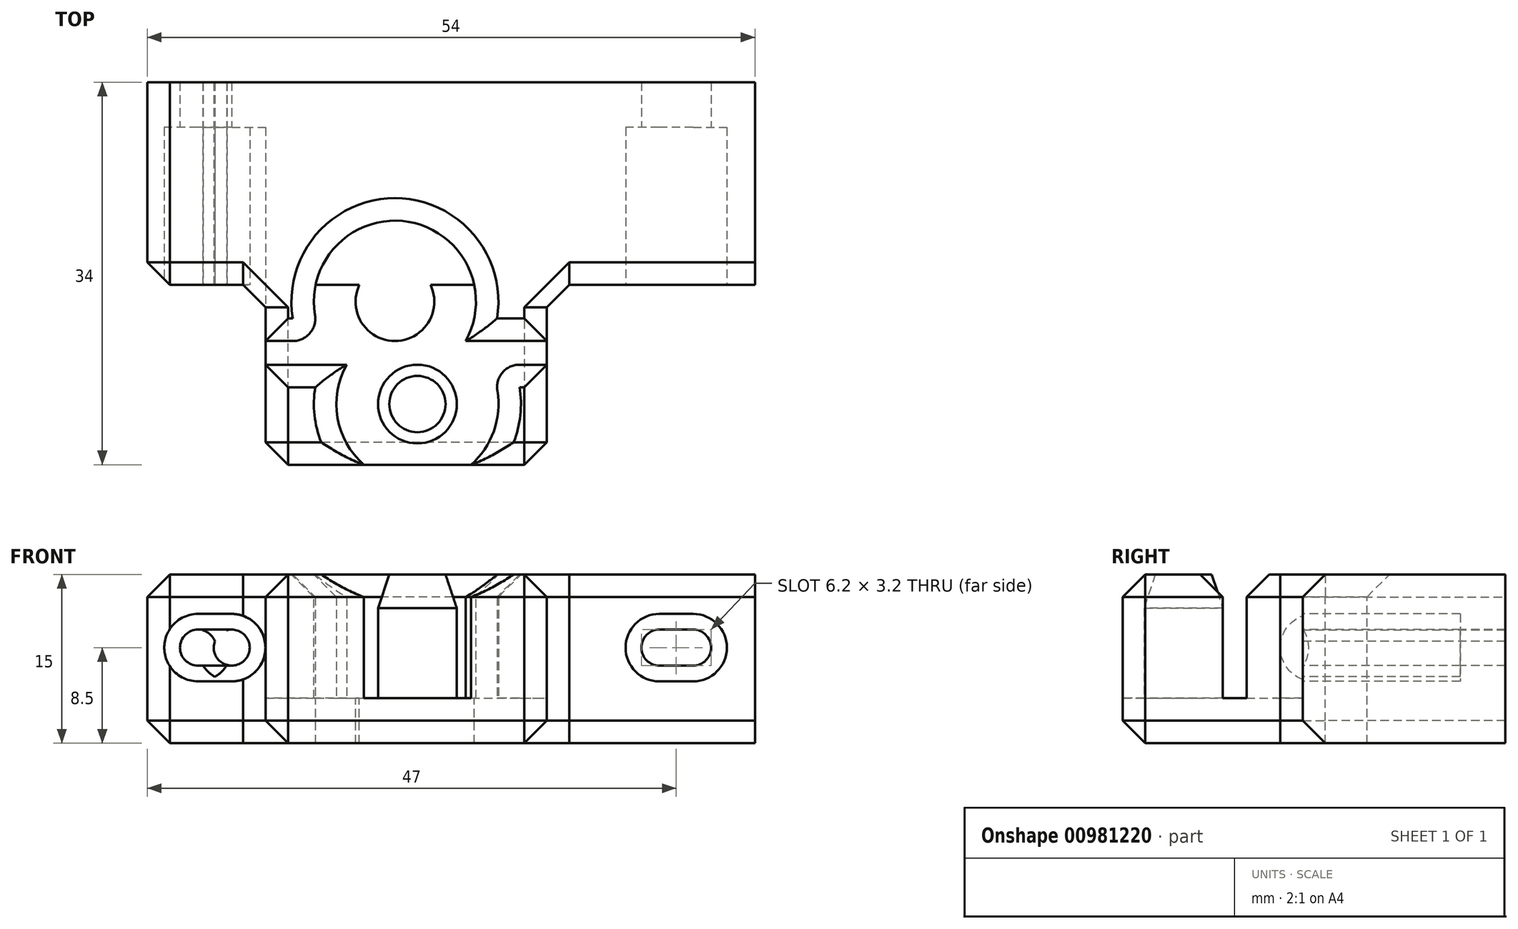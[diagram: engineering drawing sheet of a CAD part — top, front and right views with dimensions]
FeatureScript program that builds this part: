
annotation { "Feature Type Name" : "Feature", "Feature Type Description" : "" }
export const myFeature = defineFeature(function(context is Context, id is Id, definition is map)
    precondition{}
    {
        {
            var Q0;
            Q0=qCreatedBy(makeId("Top.planeOp"),FACE);
            var sketch = newSketch(context, id + "F0", { "sketchPlane" : qUnion([Q0])});
            skLineSegment(sketch, "E0.bottom", {"start": v(0, 0) * mm, "end": v(54, 0) * mm});
            skLineSegment(sketch, "E0.top", {"start": v(0, 10) * mm, "end": v(54, 10) * mm});
            skLineSegment(sketch, "E0.left", {"start": v(0, 0) * mm, "end": v(0, 10) * mm});
            skLineSegment(sketch, "E0.right", {"start": v(54, 0) * mm, "end": v(54, 10) * mm});
            skLineSegment(sketch, "E1.bottom", {"start": v(10.5, 0) * mm, "end": v(35.5, 0) * mm});
            skLineSegment(sketch, "E1.top", {"start": v(10.5, -16) * mm, "end": v(35.5, -16) * mm});
            skLineSegment(sketch, "E1.left", {"start": v(10.5, 0) * mm, "end": v(10.5, -16) * mm});
            skLineSegment(sketch, "E1.right", {"start": v(35.5, 0) * mm, "end": v(35.5, -16) * mm});
            skLineSegment(sketch, "E2", {"start": v(10.5, -5) * mm, "end": v(12.92, -5) * mm});
            skLineSegment(sketch, "E3", {"start": v(33.08, -7.1) * mm, "end": v(35.5, -7.1) * mm});
            skCircle(sketch, "E4", {"center": v(22, -1.5) * mm, "radius": 3.5 * mm});
            skCircle(sketch, "E5", {"center": v(24, -10.6) * mm, "radius": 3.5 * mm});
            skArc(sketch, "E6", {"start": v(28.76, -16) * mm, "mid": v(30.78, -13.02) * mm, "end": v(31.1, -9.43) * mm});
            skArc(sketch, "E7", {"start": v(28.3, -5) * mm, "mid": v(23.23, 5.6) * mm, "end": v(14.9, -2.67) * mm});
            skLineSegment(sketch, "E8", {"start": v(22, -1.5) * mm, "end": v(22, -19) * mm, "construction": true});
            skLineSegment(sketch, "E9", {"start": v(22, -19) * mm, "end": v(24, -19) * mm, "construction": true});
            skLineSegment(sketch, "E10", {"start": v(24, -19) * mm, "end": v(24, -10.6) * mm, "construction": true});
            skPoint(sketch, "E11", {"position": v(23, -16) * mm});
            skPoint(sketch, "E12", {"position": v(23, -19) * mm});
            skArc(sketch, "E13.trimOffspring", {"start": v(17.7, -7.1) * mm, "mid": v(16.9, -11.82) * mm, "end": v(19.24, -16) * mm});
            skPoint(sketch, "E14.newPointA", {"position": v(35.5, -5) * mm});
            skArc(sketch, "E14.filletArc", {"start": v(12.92, -5) * mm, "mid": v(14.45, -4.3) * mm, "end": v(14.9, -2.67) * mm});
            skArc(sketch, "E15.filletArc", {"start": v(33.08, -7.1) * mm, "mid": v(31.55, -7.8) * mm, "end": v(31.1, -9.43) * mm});
            skLineSegment(sketch, "E16", {"start": v(17.7, -7.1) * mm, "end": v(10.5, -7.1) * mm});
            skLineSegment(sketch, "E17", {"start": v(28.3, -5) * mm, "end": v(35.5, -5) * mm});
            skLineSegment(sketch, "E18", {"start": v(0, 10) * mm, "end": v(0, 18) * mm});
            skLineSegment(sketch, "E19", {"start": v(0, 18) * mm, "end": v(54, 18) * mm});
            skLineSegment(sketch, "E20", {"start": v(54, 18) * mm, "end": v(54, 10) * mm});
            skSolve(sketch);
        }
        {
            var Q0;
            Q0=makeQuery(id+"F0.imprint","IMPRINT",FACE,{"disambiguationData":[TD([[makeQuery(id+"F0.imprint","IMPRINT",EDGE,{"derivedFrom":sQuery(id+"F0.wireOp",EDGE,"E0.top")}),-1.0]])]});
            var Q1;
            {var subQ6=sQuery(id+"F0.wireOp",EDGE,"E2");Q1=makeQuery(id+"F0.imprint","IMPRINT",FACE,{"disambiguationData":[TD([[makeQuery(id+"F0.imprint","IMPRINT",EDGE,{"derivedFrom":subQ6}),1.0]])]});}
            var Q2;
            {var subQ3=sQuery(id+"F0.wireOp",EDGE,"E13.trimOffspring");Q2=makeQuery(id+"F0.imprint","IMPRINT",FACE,{"disambiguationData":[TD([[makeQuery(id+"F0.imprint","IMPRINT",EDGE,{"derivedFrom":subQ3}),-1.0]])]});}
            var Q3;
            {var subQ1=sQuery(id+"F0.wireOp",EDGE,"E3");Q3=makeQuery(id+"F0.imprint","IMPRINT",FACE,{"disambiguationData":[TD([[makeQuery(id+"F0.imprint","IMPRINT",EDGE,{"derivedFrom":subQ1}),-1.0]])]});}
            var Q4;
            {var subQ5=sQuery(id+"F0.wireOp",EDGE,"E17");Q4=makeQuery(id+"F0.imprint","IMPRINT",FACE,{"disambiguationData":[TD([[makeQuery(id+"F0.imprint","IMPRINT",EDGE,{"derivedFrom":subQ5}),1.0]])]});}
            var Q5;
            {var subQ13=sQuery(id+"F0.wireOp",EDGE,"E2");Q5=makeQuery(id+"F0.imprint","IMPRINT",FACE,{"disambiguationData":[TD([[makeQuery(id+"F0.imprint","IMPRINT",EDGE,{"derivedFrom":subQ13}),-1.0]])]});}
            var Q6;
            {var subQ0=sQuery(id+"F0.wireOp",EDGE,"E4");var subQ1=sQuery(id+"F0.wireOp",EDGE,"E1.bottom");var subQ2=makeQuery(id+"F0.imprint","INTERSECT",VERTEX,{"disambiguationData":[OD(0.0)],"derivedFrom":[subQ1,subQ0]});Q6=makeQuery(id+"F0.imprint","IMPRINT",FACE,{"disambiguationData":[TD([[makeQuery(id+"F0.imprint","IMPRINT",EDGE,{"disambiguationData":[TD([[subQ2,-1.0]])],"derivedFrom":subQ1}),-1.0]])]});}
            var Q7;
            Q7=makeQuery(id+"F0.imprint","IMPRINT",FACE,{"disambiguationData":[TD([[makeQuery(id+"F0.imprint","IMPRINT",EDGE,{"derivedFrom":sQuery(id+"F0.wireOp",EDGE,"E5")}),1.0]])]});
            var Q8;
            {var subQ0=sQuery(id+"F0.wireOp",EDGE,"E4");var subQ1=sQuery(id+"F0.wireOp",EDGE,"E1.bottom");var subQ2=makeQuery(id+"F0.imprint","INTERSECT",VERTEX,{"disambiguationData":[OD(0.0)],"derivedFrom":[subQ1,subQ0]});Q8=makeQuery(id+"F0.imprint","IMPRINT",FACE,{"disambiguationData":[TD([[makeQuery(id+"F0.imprint","IMPRINT",EDGE,{"disambiguationData":[TD([[subQ2,-1.0]])],"derivedFrom":subQ1}),1.0]])]});}
            var Q9;
            {var subQ0=sQuery(id+"F0.wireOp",EDGE,"E7");var subQ1=sQuery(id+"F0.wireOp",EDGE,"E1.bottom");var subQ2=makeQuery(id+"F0.imprint","INTERSECT",VERTEX,{"disambiguationData":[OD(0.0)],"derivedFrom":[subQ1,subQ0]});Q9=makeQuery(id+"F0.imprint","IMPRINT",FACE,{"disambiguationData":[TD([[makeQuery(id+"F0.imprint","IMPRINT",EDGE,{"disambiguationData":[TD([[subQ2,-1.0]])],"derivedFrom":subQ1}),1.0]])]});}
            var Q10;
            Q10=makeQuery(id+"F0.imprint","IMPRINT",FACE,{"disambiguationData":[TD([[makeQuery(id+"F0.imprint","IMPRINT",EDGE,{"derivedFrom":sQuery(id+"F0.wireOp",EDGE,"E0.top")}),1.0]])]});
            extrude(context, id + "F1", {"entities" : qUnion([Q0, Q1, Q2, Q3, Q4, Q5, Q6, Q7, Q8, Q9, Q10]), "oppositeDirection" : true, "depth" : 4 * mm, "offsetDistance" : 25 * mm});
        }
        {
            var Q0;
            Q0=makeQuery(id+"F0.imprint","IMPRINT",FACE,{"disambiguationData":[TD([[makeQuery(id+"F0.imprint","IMPRINT",EDGE,{"derivedFrom":sQuery(id+"F0.wireOp",EDGE,"E0.top")}),-1.0]])]});
            var Q1;
            {var subQ5=sQuery(id+"F0.wireOp",EDGE,"E17");Q1=makeQuery(id+"F0.imprint","IMPRINT",FACE,{"disambiguationData":[TD([[makeQuery(id+"F0.imprint","IMPRINT",EDGE,{"derivedFrom":subQ5}),1.0]])]});}
            var Q2;
            {var subQ6=sQuery(id+"F0.wireOp",EDGE,"E2");Q2=makeQuery(id+"F0.imprint","IMPRINT",FACE,{"disambiguationData":[TD([[makeQuery(id+"F0.imprint","IMPRINT",EDGE,{"derivedFrom":subQ6}),1.0]])]});}
            var Q3;
            {var subQ3=sQuery(id+"F0.wireOp",EDGE,"E13.trimOffspring");Q3=makeQuery(id+"F0.imprint","IMPRINT",FACE,{"disambiguationData":[TD([[makeQuery(id+"F0.imprint","IMPRINT",EDGE,{"derivedFrom":subQ3}),-1.0]])]});}
            var Q4;
            {var subQ1=sQuery(id+"F0.wireOp",EDGE,"E3");Q4=makeQuery(id+"F0.imprint","IMPRINT",FACE,{"disambiguationData":[TD([[makeQuery(id+"F0.imprint","IMPRINT",EDGE,{"derivedFrom":subQ1}),-1.0]])]});}
            var Q5;
            Q5=makeQuery(id+"F0.imprint","IMPRINT",FACE,{"disambiguationData":[TD([[makeQuery(id+"F0.imprint","IMPRINT",EDGE,{"derivedFrom":sQuery(id+"F0.wireOp",EDGE,"E5")}),1.0]])]});
            var Q6;
            {var subQ0=sQuery(id+"F0.wireOp",EDGE,"E4");var subQ1=sQuery(id+"F0.wireOp",EDGE,"E1.bottom");var subQ2=makeQuery(id+"F0.imprint","INTERSECT",VERTEX,{"disambiguationData":[OD(0.0)],"derivedFrom":[subQ1,subQ0]});Q6=makeQuery(id+"F0.imprint","IMPRINT",FACE,{"disambiguationData":[TD([[makeQuery(id+"F0.imprint","IMPRINT",EDGE,{"disambiguationData":[TD([[subQ2,-1.0]])],"derivedFrom":subQ1}),-1.0]])]});}
            var Q7;
            {var subQ0=sQuery(id+"F0.wireOp",EDGE,"E4");var subQ1=sQuery(id+"F0.wireOp",EDGE,"E1.bottom");var subQ2=makeQuery(id+"F0.imprint","INTERSECT",VERTEX,{"disambiguationData":[OD(0.0)],"derivedFrom":[subQ1,subQ0]});Q7=makeQuery(id+"F0.imprint","IMPRINT",FACE,{"disambiguationData":[TD([[makeQuery(id+"F0.imprint","IMPRINT",EDGE,{"disambiguationData":[TD([[subQ2,-1.0]])],"derivedFrom":subQ1}),1.0]])]});}
            var Q8;
            Q8=makeQuery(id+"F0.imprint","IMPRINT",FACE,{"disambiguationData":[TD([[makeQuery(id+"F0.imprint","IMPRINT",EDGE,{"derivedFrom":sQuery(id+"F0.wireOp",EDGE,"E0.top")}),1.0]])]});
            extrude(context, id + "F2", {"entities" : qUnion([Q0, Q1, Q2, Q3, Q4, Q5, Q6, Q7, Q8]), "operationType" : NewBodyOperationType.ADD, "depth" : 11 * mm, "offsetDistance" : 25 * mm});
        }
        {
            var Q0;
            Q0=makeQuery(id+"F2.opExtrude","CAP_EDGE",EDGE,{"disambiguationData":[OSD([sQuery(id+"F0.wireOp",EDGE,"E2")])],"isStart":false});
            var Q1;
            Q1=makeQuery(id+"F2.opExtrude","CAP_EDGE",EDGE,{"disambiguationData":[OSD([sQuery(id+"F0.wireOp",EDGE,"E17")])],"isStart":false});
            var Q2;
            Q2=makeQuery(id+"F2.opExtrude","CAP_EDGE",EDGE,{"disambiguationData":[OSD([sQuery(id+"F0.wireOp",EDGE,"E3")])],"isStart":false});
            var Q3;
            Q3=makeQuery(id+"F2.opExtrude","CAP_EDGE",EDGE,{"disambiguationData":[OSD([sQuery(id+"F0.wireOp",EDGE,"E13.trimOffspring")])],"isStart":false});
            var Q4;
            Q4=makeQuery(id+"F2.opExtrude","CAP_EDGE",EDGE,{"disambiguationData":[OSD([sQuery(id+"F0.wireOp",EDGE,"E16")])],"isStart":false});
            chamfer(context, id + "F3", {"entities" : qUnion([Q0, Q1, Q2, Q3, Q4]), "width" : 2 * mm, "tangentPropagation" : true});
        }
        {
            var Q0;
            Q0=makeQuery(id+"F2.opExtrude","CAP_FACE",FACE,{"disambiguationData":[OSD([sQuery(id+"F0.wireOp",EDGE,"E4")])],"isStart":false});
            var Q1;
            Q1=makeQuery(id+"F2.opExtrude","CAP_EDGE",EDGE,{"disambiguationData":[OSD([sQuery(id+"F0.wireOp",EDGE,"E5")])],"isStart":false});
            chamfer(context, id + "F4", {"entities" : qUnion([Q0, Q1]), "chamferType" : ChamferType.TWO_OFFSETS, "width1" : 1 * mm, "oppositeDirection" : false, "width2" : 3 * mm, "tangentPropagation" : true});
        }
        {
            var Q0;
            {var subQ0=sQuery(id+"F0.wireOp",EDGE,"E0.bottom");var subQ1=makeQuery(id+"F0.imprint","IMPRINT",EDGE,{"disambiguationData":[TD([[makeQuery(id+"F0.imprint","INTERSECT",VERTEX,{"derivedFrom":[subQ0,sQuery(id+"F0.wireOp",EDGE,"E0.right")]}),1.0]])],"derivedFrom":subQ0});Q0=makeQuery(id+"F2.boolean.opBoolean","MERGE",FACE,{"derivedFrom":[makeQuery(id+"F1.opExtrude","SWEPT_FACE",FACE,{"disambiguationData":[OSD([subQ0]),TDD([subQ1])]}),makeQuery(id+"F2.opExtrude","SWEPT_FACE",FACE,{"disambiguationData":[OSD([subQ0]),TDD([subQ1])]})]});}
            var sketch = newSketch(context, id + "F5", { "sketchPlane" : qUnion([Q0])});
            skCircle(sketch, "E21", {"center": v(4.5, 4.5) * mm, "radius": 1.6 * mm});
            skCircle(sketch, "E22", {"center": v(4.5, 4.5) * mm, "radius": 3 * mm});
            skCircle(sketch, "E23", {"center": v(48.5, 4.5) * mm, "radius": 1.6 * mm});
            skCircle(sketch, "E24", {"center": v(48.5, 4.5) * mm, "radius": 3 * mm});
            skCircle(sketch, "E25", {"center": v(7.5, 4.5) * mm, "radius": 1.6 * mm});
            skCircle(sketch, "E26", {"center": v(7.5, 4.5) * mm, "radius": 3 * mm});
            skCircle(sketch, "E27", {"center": v(45.5, 4.5) * mm, "radius": 1.6 * mm});
            skCircle(sketch, "E28", {"center": v(45.5, 4.5) * mm, "radius": 3 * mm});
            skLineSegment(sketch, "E29", {"start": v(4.5, 6.1) * mm, "end": v(7.5, 6.1) * mm});
            skLineSegment(sketch, "E30", {"start": v(7.5, 2.9) * mm, "end": v(4.5, 2.9) * mm});
            skLineSegment(sketch, "E31", {"start": v(45.5, 2.9) * mm, "end": v(48.5, 2.9) * mm});
            skLineSegment(sketch, "E32", {"start": v(48.5, 6.1) * mm, "end": v(45.5, 6.1) * mm});
            skLineSegment(sketch, "E33", {"start": v(45.5, 7.5) * mm, "end": v(48.5, 7.5) * mm});
            skLineSegment(sketch, "E34", {"start": v(48.5, 1.5) * mm, "end": v(45.5, 1.5) * mm});
            skLineSegment(sketch, "E35", {"start": v(7.5, 7.5) * mm, "end": v(4.5, 7.5) * mm});
            skLineSegment(sketch, "E36", {"start": v(4.5, 1.5) * mm, "end": v(7.5, 1.5) * mm});
            skSolve(sketch);
        }
        {
            var Q0;
            {var subQ0=sQuery(id+"F5.wireOp",EDGE,"E21");var subQ1=makeQuery(id+"F5.imprint","INTERSECT",VERTEX,{"derivedFrom":[subQ0,sQuery(id+"F5.wireOp",EDGE,"E29")]});Q0=makeQuery(id+"F5.imprint","IMPRINT",FACE,{"disambiguationData":[TD([[makeQuery(id+"F5.imprint","IMPRINT",EDGE,{"disambiguationData":[TD([[subQ1,1.0]])],"derivedFrom":subQ0}),1.0]])]});}
            var Q1;
            {var subQ0=sQuery(id+"F5.wireOp",EDGE,"E26");var subQ1=sQuery(id+"F5.wireOp",EDGE,"E21");var subQ2=makeQuery(id+"F5.imprint","INTERSECT",VERTEX,{"disambiguationData":[OD(0.0)],"derivedFrom":[subQ1,subQ0]});Q1=makeQuery(id+"F5.imprint","IMPRINT",FACE,{"disambiguationData":[TD([[makeQuery(id+"F5.imprint","IMPRINT",EDGE,{"disambiguationData":[TD([[subQ2,1.0]])],"derivedFrom":subQ1}),1.0]])]});}
            var Q2;
            {var subQ0=sQuery(id+"F5.wireOp",EDGE,"E25");var subQ1=sQuery(id+"F5.wireOp",EDGE,"E21");var subQ2=makeQuery(id+"F5.imprint","INTERSECT",VERTEX,{"disambiguationData":[OD(0.0)],"derivedFrom":[subQ1,subQ0]});Q2=makeQuery(id+"F5.imprint","IMPRINT",FACE,{"disambiguationData":[TD([[makeQuery(id+"F5.imprint","IMPRINT",EDGE,{"disambiguationData":[TD([[subQ2,1.0]])],"derivedFrom":subQ1}),-1.0]])]});}
            var Q3;
            {var subQ1=sQuery(id+"F5.wireOp",EDGE,"E21");var subQ5=sQuery(id+"F5.wireOp",EDGE,"E26");var subQ6=makeQuery(id+"F5.imprint","INTERSECT",VERTEX,{"disambiguationData":[OD(0.0)],"derivedFrom":[subQ1,subQ5]});Q3=makeQuery(id+"F5.imprint","IMPRINT",FACE,{"disambiguationData":[TD([[makeQuery(id+"F5.imprint","IMPRINT",EDGE,{"disambiguationData":[TD([[subQ6,1.0]])],"derivedFrom":subQ1}),-1.0]])]});}
            var Q4;
            {var subQ0=sQuery(id+"F5.wireOp",EDGE,"E25");var subQ1=sQuery(id+"F5.wireOp",EDGE,"E21");var subQ2=makeQuery(id+"F5.imprint","INTERSECT",VERTEX,{"disambiguationData":[OD(0.0)],"derivedFrom":[subQ1,subQ0]});Q4=makeQuery(id+"F5.imprint","IMPRINT",FACE,{"disambiguationData":[TD([[makeQuery(id+"F5.imprint","IMPRINT",EDGE,{"disambiguationData":[TD([[subQ2,1.0]])],"derivedFrom":subQ1}),1.0]])]});}
            var Q5;
            {var subQ0=sQuery(id+"F5.wireOp",EDGE,"E26");var subQ1=sQuery(id+"F5.wireOp",EDGE,"E21");var subQ2=makeQuery(id+"F5.imprint","INTERSECT",VERTEX,{"disambiguationData":[OD(1.0)],"derivedFrom":[subQ1,subQ0]});Q5=makeQuery(id+"F5.imprint","IMPRINT",FACE,{"disambiguationData":[TD([[makeQuery(id+"F5.imprint","IMPRINT",EDGE,{"disambiguationData":[TD([[subQ2,-1.0]])],"derivedFrom":subQ1}),-1.0]])]});}
            var Q6;
            {var subQ0=sQuery(id+"F5.wireOp",EDGE,"E25");var subQ1=sQuery(id+"F5.wireOp",EDGE,"E22");var subQ2=makeQuery(id+"F5.imprint","INTERSECT",VERTEX,{"disambiguationData":[OD(0.0)],"derivedFrom":[subQ1,subQ0]});Q6=makeQuery(id+"F5.imprint","IMPRINT",FACE,{"disambiguationData":[TD([[makeQuery(id+"F5.imprint","IMPRINT",EDGE,{"disambiguationData":[TD([[subQ2,1.0]])],"derivedFrom":subQ1}),-1.0]])]});}
            var Q7;
            {var subQ0=sQuery(id+"F5.wireOp",EDGE,"E30");var subQ1=sQuery(id+"F5.wireOp",EDGE,"E22");var subQ2=makeQuery(id+"F5.imprint","INTERSECT",VERTEX,{"derivedFrom":[subQ1,subQ0]});Q7=makeQuery(id+"F5.imprint","IMPRINT",FACE,{"disambiguationData":[TD([[makeQuery(id+"F5.imprint","IMPRINT",EDGE,{"disambiguationData":[TD([[subQ2,-1.0]])],"derivedFrom":subQ1}),-1.0]])]});}
            var Q8;
            {var subQ0=sQuery(id+"F5.wireOp",EDGE,"E30");var subQ1=sQuery(id+"F5.wireOp",EDGE,"E21");var subQ2=makeQuery(id+"F5.imprint","INTERSECT",VERTEX,{"derivedFrom":[subQ1,subQ0]});Q8=makeQuery(id+"F5.imprint","IMPRINT",FACE,{"disambiguationData":[TD([[makeQuery(id+"F5.imprint","IMPRINT",EDGE,{"disambiguationData":[TD([[subQ2,-1.0]])],"derivedFrom":subQ1}),-1.0]])]});}
            var Q9;
            {var subQ0=sQuery(id+"F5.wireOp",EDGE,"E29");var subQ1=sQuery(id+"F5.wireOp",EDGE,"E21");var subQ2=makeQuery(id+"F5.imprint","INTERSECT",VERTEX,{"derivedFrom":[subQ1,subQ0]});Q9=makeQuery(id+"F5.imprint","IMPRINT",FACE,{"disambiguationData":[TD([[makeQuery(id+"F5.imprint","IMPRINT",EDGE,{"disambiguationData":[TD([[subQ2,1.0]])],"derivedFrom":subQ1}),-1.0]])]});}
            var Q10;
            {var subQ0=sQuery(id+"F5.wireOp",EDGE,"E29");var subQ1=sQuery(id+"F5.wireOp",EDGE,"E22");var subQ2=makeQuery(id+"F5.imprint","INTERSECT",VERTEX,{"derivedFrom":[subQ1,subQ0]});Q10=makeQuery(id+"F5.imprint","IMPRINT",FACE,{"disambiguationData":[TD([[makeQuery(id+"F5.imprint","IMPRINT",EDGE,{"disambiguationData":[TD([[subQ2,1.0]])],"derivedFrom":subQ1}),-1.0]])]});}
            var Q11;
            {var subQ0=sQuery(id+"F5.wireOp",EDGE,"E27");var subQ1=sQuery(id+"F5.wireOp",EDGE,"E23");var subQ2=makeQuery(id+"F5.imprint","INTERSECT",VERTEX,{"disambiguationData":[OD(0.0)],"derivedFrom":[subQ1,subQ0]});Q11=makeQuery(id+"F5.imprint","IMPRINT",FACE,{"disambiguationData":[TD([[makeQuery(id+"F5.imprint","IMPRINT",EDGE,{"disambiguationData":[TD([[subQ2,-1.0]])],"derivedFrom":subQ1}),1.0]])]});}
            var Q12;
            {var subQ0=sQuery(id+"F5.wireOp",EDGE,"E28");var subQ1=sQuery(id+"F5.wireOp",EDGE,"E23");var subQ2=makeQuery(id+"F5.imprint","INTERSECT",VERTEX,{"disambiguationData":[OD(0.0)],"derivedFrom":[subQ1,subQ0]});Q12=makeQuery(id+"F5.imprint","IMPRINT",FACE,{"disambiguationData":[TD([[makeQuery(id+"F5.imprint","IMPRINT",EDGE,{"disambiguationData":[TD([[subQ2,-1.0]])],"derivedFrom":subQ1}),1.0]])]});}
            var Q13;
            {var subQ0=sQuery(id+"F5.wireOp",EDGE,"E28");var subQ1=sQuery(id+"F5.wireOp",EDGE,"E23");var subQ2=makeQuery(id+"F5.imprint","INTERSECT",VERTEX,{"disambiguationData":[OD(0.0)],"derivedFrom":[subQ1,subQ0]});Q13=makeQuery(id+"F5.imprint","IMPRINT",FACE,{"disambiguationData":[TD([[makeQuery(id+"F5.imprint","IMPRINT",EDGE,{"disambiguationData":[TD([[subQ2,-1.0]])],"derivedFrom":subQ1}),-1.0]])]});}
            var Q14;
            {var subQ0=sQuery(id+"F5.wireOp",EDGE,"E27");var subQ1=sQuery(id+"F5.wireOp",EDGE,"E23");var subQ2=makeQuery(id+"F5.imprint","INTERSECT",VERTEX,{"disambiguationData":[OD(0.0)],"derivedFrom":[subQ1,subQ0]});Q14=makeQuery(id+"F5.imprint","IMPRINT",FACE,{"disambiguationData":[TD([[makeQuery(id+"F5.imprint","IMPRINT",EDGE,{"disambiguationData":[TD([[subQ2,-1.0]])],"derivedFrom":subQ1}),-1.0]])]});}
            var Q15;
            {var subQ0=sQuery(id+"F5.wireOp",EDGE,"E27");var subQ1=sQuery(id+"F5.wireOp",EDGE,"E23");var subQ2=makeQuery(id+"F5.imprint","INTERSECT",VERTEX,{"disambiguationData":[OD(1.0)],"derivedFrom":[subQ1,subQ0]});Q15=makeQuery(id+"F5.imprint","IMPRINT",FACE,{"disambiguationData":[TD([[makeQuery(id+"F5.imprint","IMPRINT",EDGE,{"disambiguationData":[TD([[subQ2,-1.0]])],"derivedFrom":subQ1}),-1.0]])]});}
            var Q16;
            {var subQ0=sQuery(id+"F5.wireOp",EDGE,"E27");var subQ1=sQuery(id+"F5.wireOp",EDGE,"E24");var subQ2=makeQuery(id+"F5.imprint","INTERSECT",VERTEX,{"disambiguationData":[OD(0.0)],"derivedFrom":[subQ1,subQ0]});Q16=makeQuery(id+"F5.imprint","IMPRINT",FACE,{"disambiguationData":[TD([[makeQuery(id+"F5.imprint","IMPRINT",EDGE,{"disambiguationData":[TD([[subQ2,-1.0]])],"derivedFrom":subQ1}),-1.0]])]});}
            var Q17;
            {var subQ0=sQuery(id+"F5.wireOp",EDGE,"E23");var subQ1=makeQuery(id+"F5.imprint","INTERSECT",VERTEX,{"derivedFrom":[subQ0,sQuery(id+"F5.wireOp",EDGE,"E32")]});Q17=makeQuery(id+"F5.imprint","IMPRINT",FACE,{"disambiguationData":[TD([[makeQuery(id+"F5.imprint","IMPRINT",EDGE,{"disambiguationData":[TD([[subQ1,-1.0]])],"derivedFrom":subQ0}),1.0]])]});}
            var Q18;
            {var subQ0=sQuery(id+"F5.wireOp",EDGE,"E31");var subQ1=sQuery(id+"F5.wireOp",EDGE,"E23");var subQ2=makeQuery(id+"F5.imprint","INTERSECT",VERTEX,{"derivedFrom":[subQ1,subQ0]});Q18=makeQuery(id+"F5.imprint","IMPRINT",FACE,{"disambiguationData":[TD([[makeQuery(id+"F5.imprint","IMPRINT",EDGE,{"disambiguationData":[TD([[subQ2,1.0]])],"derivedFrom":subQ1}),-1.0]])]});}
            var Q19;
            {var subQ0=sQuery(id+"F5.wireOp",EDGE,"E27");var subQ1=sQuery(id+"F5.wireOp",EDGE,"E24");var subQ2=makeQuery(id+"F5.imprint","INTERSECT",VERTEX,{"disambiguationData":[OD(1.0)],"derivedFrom":[subQ1,subQ0]});Q19=makeQuery(id+"F5.imprint","IMPRINT",FACE,{"disambiguationData":[TD([[makeQuery(id+"F5.imprint","IMPRINT",EDGE,{"disambiguationData":[TD([[subQ2,-1.0]])],"derivedFrom":subQ1}),-1.0]])]});}
            var Q20;
            {var subQ0=sQuery(id+"F5.wireOp",EDGE,"E32");var subQ1=sQuery(id+"F5.wireOp",EDGE,"E24");var subQ2=makeQuery(id+"F5.imprint","INTERSECT",VERTEX,{"derivedFrom":[subQ1,subQ0]});Q20=makeQuery(id+"F5.imprint","IMPRINT",FACE,{"disambiguationData":[TD([[makeQuery(id+"F5.imprint","IMPRINT",EDGE,{"disambiguationData":[TD([[subQ2,-1.0]])],"derivedFrom":subQ1}),-1.0]])]});}
            var Q21;
            {var subQ0=sQuery(id+"F5.wireOp",EDGE,"E32");var subQ1=sQuery(id+"F5.wireOp",EDGE,"E23");var subQ2=makeQuery(id+"F5.imprint","INTERSECT",VERTEX,{"derivedFrom":[subQ1,subQ0]});Q21=makeQuery(id+"F5.imprint","IMPRINT",FACE,{"disambiguationData":[TD([[makeQuery(id+"F5.imprint","IMPRINT",EDGE,{"disambiguationData":[TD([[subQ2,-1.0]])],"derivedFrom":subQ1}),-1.0]])]});}
            extrude(context, id + "F6", {"entities" : qUnion([Q0, Q1, Q2, Q3, Q4, Q5, Q6, Q7, Q8, Q9, Q10, Q11, Q12, Q13, Q14, Q15, Q16, Q17, Q18, Q19, Q20, Q21]), "operationType" : NewBodyOperationType.REMOVE, "endBound" : BoundingType.THROUGH_ALL, "oppositeDirection" : true, "depth" : 25 * mm, "offsetDistance" : 25 * mm});
        }
        {
            var Q0;
            {var subQ6=sQuery(id+"F5.wireOp",EDGE,"E29");var subQ7=sQuery(id+"F5.wireOp",EDGE,"E21");var subQ8=makeQuery(id+"F5.imprint","INTERSECT",VERTEX,{"derivedFrom":[subQ7,subQ6]});Q0=makeQuery(id+"F5.imprint","IMPRINT",FACE,{"disambiguationData":[TD([[makeQuery(id+"F5.imprint","IMPRINT",EDGE,{"disambiguationData":[TD([[subQ8,-1.0]])],"derivedFrom":subQ7}),-1.0]])]});}
            var Q1;
            {var subQ2=sQuery(id+"F5.wireOp",EDGE,"E22");var subQ4=sQuery(id+"F5.wireOp",EDGE,"E29");var subQ11=makeQuery(id+"F5.imprint","INTERSECT",VERTEX,{"derivedFrom":[subQ2,subQ4]});Q1=makeQuery(id+"F5.imprint","IMPRINT",FACE,{"disambiguationData":[TD([[makeQuery(id+"F5.imprint","IMPRINT",EDGE,{"disambiguationData":[TD([[subQ11,-1.0]])],"derivedFrom":subQ2}),-1.0]])]});}
            var Q2;
            {var subQ0=sQuery(id+"F5.wireOp",EDGE,"E29");var subQ1=sQuery(id+"F5.wireOp",EDGE,"E22");var subQ2=makeQuery(id+"F5.imprint","INTERSECT",VERTEX,{"derivedFrom":[subQ1,subQ0]});Q2=makeQuery(id+"F5.imprint","IMPRINT",FACE,{"disambiguationData":[TD([[makeQuery(id+"F5.imprint","IMPRINT",EDGE,{"disambiguationData":[TD([[subQ2,-1.0]])],"derivedFrom":subQ1}),1.0]])]});}
            var Q3;
            {var subQ0=sQuery(id+"F5.wireOp",EDGE,"E26");var subQ1=sQuery(id+"F5.wireOp",EDGE,"E22");var subQ2=makeQuery(id+"F5.imprint","INTERSECT",VERTEX,{"disambiguationData":[OD(1.0)],"derivedFrom":[subQ1,subQ0]});Q3=makeQuery(id+"F5.imprint","IMPRINT",FACE,{"disambiguationData":[TD([[makeQuery(id+"F5.imprint","IMPRINT",EDGE,{"disambiguationData":[TD([[subQ2,-1.0]])],"derivedFrom":subQ1}),1.0]])]});}
            var Q4;
            {var subQ0=sQuery(id+"F5.wireOp",EDGE,"E36");Q4=makeQuery(id+"F5.imprint","IMPRINT",FACE,{"disambiguationData":[TD([[makeQuery(id+"F5.imprint","IMPRINT",EDGE,{"derivedFrom":subQ0}),1.0]])]});}
            var Q5;
            {var subQ0=sQuery(id+"F5.wireOp",EDGE,"E35");Q5=makeQuery(id+"F5.imprint","IMPRINT",FACE,{"disambiguationData":[TD([[makeQuery(id+"F5.imprint","IMPRINT",EDGE,{"derivedFrom":subQ0}),1.0]])]});}
            var Q6;
            {var subQ0=sQuery(id+"F5.wireOp",EDGE,"E31");var subQ1=sQuery(id+"F5.wireOp",EDGE,"E24");var subQ2=makeQuery(id+"F5.imprint","INTERSECT",VERTEX,{"derivedFrom":[subQ1,subQ0]});Q6=makeQuery(id+"F5.imprint","IMPRINT",FACE,{"disambiguationData":[TD([[makeQuery(id+"F5.imprint","IMPRINT",EDGE,{"disambiguationData":[TD([[subQ2,-1.0]])],"derivedFrom":subQ1}),1.0]])]});}
            var Q7;
            {var subQ0=sQuery(id+"F5.wireOp",EDGE,"E28");var subQ1=sQuery(id+"F5.wireOp",EDGE,"E24");var subQ2=makeQuery(id+"F5.imprint","INTERSECT",VERTEX,{"disambiguationData":[OD(0.0)],"derivedFrom":[subQ1,subQ0]});Q7=makeQuery(id+"F5.imprint","IMPRINT",FACE,{"disambiguationData":[TD([[makeQuery(id+"F5.imprint","IMPRINT",EDGE,{"disambiguationData":[TD([[subQ2,-1.0]])],"derivedFrom":subQ1}),1.0]])]});}
            var Q8;
            {var subQ0=sQuery(id+"F5.wireOp",EDGE,"E33");Q8=makeQuery(id+"F5.imprint","IMPRINT",FACE,{"disambiguationData":[TD([[makeQuery(id+"F5.imprint","IMPRINT",EDGE,{"derivedFrom":subQ0}),-1.0]])]});}
            var Q9;
            {var subQ0=sQuery(id+"F5.wireOp",EDGE,"E34");Q9=makeQuery(id+"F5.imprint","IMPRINT",FACE,{"disambiguationData":[TD([[makeQuery(id+"F5.imprint","IMPRINT",EDGE,{"derivedFrom":subQ0}),-1.0]])]});}
            var Q10;
            {var subQ8=sQuery(id+"F5.wireOp",EDGE,"E31");var subQ10=sQuery(id+"F5.wireOp",EDGE,"E23");var subQ11=makeQuery(id+"F5.imprint","INTERSECT",VERTEX,{"derivedFrom":[subQ10,subQ8]});Q10=makeQuery(id+"F5.imprint","IMPRINT",FACE,{"disambiguationData":[TD([[makeQuery(id+"F5.imprint","IMPRINT",EDGE,{"disambiguationData":[TD([[subQ11,-1.0]])],"derivedFrom":subQ10}),-1.0]])]});}
            var Q11;
            {var subQ5=sQuery(id+"F5.wireOp",EDGE,"E28");var subQ7=sQuery(id+"F5.wireOp",EDGE,"E24");var subQ8=makeQuery(id+"F5.imprint","INTERSECT",VERTEX,{"disambiguationData":[OD(0.0)],"derivedFrom":[subQ7,subQ5]});Q11=makeQuery(id+"F5.imprint","IMPRINT",FACE,{"disambiguationData":[TD([[makeQuery(id+"F5.imprint","IMPRINT",EDGE,{"disambiguationData":[TD([[subQ8,-1.0]])],"derivedFrom":subQ7}),-1.0]])]});}
            extrude(context, id + "F7", {"entities" : qUnion([Q0, Q1, Q2, Q3, Q4, Q5, Q6, Q7, Q8, Q9, Q10, Q11]), "operationType" : NewBodyOperationType.REMOVE, "oppositeDirection" : true, "depth" : 14 * mm, "offsetDistance" : 25 * mm});
        }
        {
            var Q0;
            {var subQ0=sQuery(id+"F0.wireOp",EDGE,"E1.left");var subQ1=sQuery(id+"F0.wireOp",EDGE,"E1.top");Q0=makeQuery(id+"F2.boolean.opBoolean","MERGE",EDGE,{"derivedFrom":[makeQuery(id+"F1.opExtrude","SWEPT_EDGE",EDGE,{"disambiguationData":[OSD([subQ1,subQ0])]}),makeQuery(id+"F2.opExtrude","SWEPT_EDGE",EDGE,{"disambiguationData":[OSD([subQ1,subQ0])]})]});}
            var Q1;
            {var subQ0=sQuery(id+"F0.wireOp",EDGE,"E1.right");var subQ1=sQuery(id+"F0.wireOp",EDGE,"E1.top");Q1=makeQuery(id+"F2.boolean.opBoolean","MERGE",EDGE,{"derivedFrom":[makeQuery(id+"F1.opExtrude","SWEPT_EDGE",EDGE,{"disambiguationData":[OSD([subQ1,subQ0])]}),makeQuery(id+"F2.opExtrude","SWEPT_EDGE",EDGE,{"disambiguationData":[OSD([subQ1,subQ0])]})]});}
            var Q2;
            {var subQ0=sQuery(id+"F0.wireOp",EDGE,"E1.right");var subQ1=sQuery(id+"F0.wireOp",EDGE,"E1.bottom");var subQ2=sQuery(id+"F0.wireOp",EDGE,"E0.bottom");Q2=makeQuery(id+"F2.boolean.opBoolean","MERGE",EDGE,{"derivedFrom":[makeQuery(id+"F1.opExtrude","SWEPT_EDGE",EDGE,{"disambiguationData":[OSD([subQ2,subQ1,subQ0])]}),makeQuery(id+"F2.opExtrude","SWEPT_EDGE",EDGE,{"disambiguationData":[OSD([subQ2,subQ1,subQ0])]})]});}
            var Q3;
            {var subQ0=sQuery(id+"F0.wireOp",EDGE,"E0.left");var subQ1=sQuery(id+"F0.wireOp",EDGE,"E0.bottom");var subQ2=sQuery(id+"F0.wireOp",EDGE,"E1.left");var subQ3=sQuery(id+"F0.wireOp",EDGE,"E1.bottom");var subQ6=sQuery(id+"F0.wireOp",EDGE,"E2");Q3=makeQuery(id+"F7.boolean.opBoolean","SPLIT",EDGE,{"disambiguationData":[TD([makeQuery(id+"F2.opExtrude","CAP_FACE",FACE,{"disambiguationData":[OSD([subQ1,sQuery(id+"F0.wireOp",EDGE,"E0.top"),subQ0,sQuery(id+"F0.wireOp",EDGE,"E0.right"),subQ2,sQuery(id+"F0.wireOp",EDGE,"E1.right"),subQ6,sQuery(id+"F0.wireOp",EDGE,"E7"),sQuery(id+"F0.wireOp",EDGE,"E14.filletArc"),sQuery(id+"F0.wireOp",EDGE,"E17")])],"isStart":false})])],"derivedFrom":makeQuery(id+"F2.boolean.opBoolean","MERGE",EDGE,{"derivedFrom":[makeQuery(id+"F1.opExtrude","SWEPT_EDGE",EDGE,{"disambiguationData":[OSD([subQ1,subQ3,subQ2])]}),makeQuery(id+"F2.opExtrude","SWEPT_EDGE",EDGE,{"disambiguationData":[OSD([subQ1,subQ3,subQ2])]})]})});}
            var Q4;
            {var subQ0=sQuery(id+"F0.wireOp",EDGE,"E0.left");var subQ1=sQuery(id+"F0.wireOp",EDGE,"E0.bottom");Q4=makeQuery(id+"F2.boolean.opBoolean","MERGE",EDGE,{"derivedFrom":[makeQuery(id+"F1.opExtrude","SWEPT_EDGE",EDGE,{"disambiguationData":[OSD([subQ1,subQ0])]}),makeQuery(id+"F2.opExtrude","SWEPT_EDGE",EDGE,{"disambiguationData":[OSD([subQ1,subQ0])]})]});}
            var Q5;
            {var subQ0=sQuery(id+"F0.wireOp",EDGE,"E0.bottom");Q5=makeQuery(id+"F2.opExtrude","CAP_EDGE",EDGE,{"disambiguationData":[OSD([subQ0]),TDD([makeQuery(id+"F0.imprint","IMPRINT",EDGE,{"disambiguationData":[TD([[makeQuery(id+"F0.imprint","INTERSECT",VERTEX,{"derivedFrom":[subQ0,sQuery(id+"F0.wireOp",EDGE,"E0.right")]}),1.0]])],"derivedFrom":subQ0})])],"isStart":false});}
            var Q6;
            {var subQ0=sQuery(id+"F0.wireOp",EDGE,"E0.bottom");Q6=makeQuery(id+"F1.opExtrude","CAP_EDGE",EDGE,{"disambiguationData":[OSD([subQ0]),TDD([makeQuery(id+"F0.imprint","IMPRINT",EDGE,{"disambiguationData":[TD([[makeQuery(id+"F0.imprint","INTERSECT",VERTEX,{"derivedFrom":[subQ0,sQuery(id+"F0.wireOp",EDGE,"E0.right")]}),1.0]])],"derivedFrom":subQ0})])],"isStart":false});}
            var Q7;
            Q7=makeQuery(id+"F1.opExtrude","CAP_EDGE",EDGE,{"disambiguationData":[OSD([sQuery(id+"F0.wireOp",EDGE,"E1.top")])],"isStart":false});
            var Q8;
            Q8=makeQuery(id+"F1.opExtrude","CAP_EDGE",EDGE,{"disambiguationData":[OSD([sQuery(id+"F0.wireOp",EDGE,"E1.left")])],"isStart":false});
            var Q9;
            Q9=makeQuery(id+"F1.opExtrude","CAP_EDGE",EDGE,{"disambiguationData":[OSD([sQuery(id+"F0.wireOp",EDGE,"E0.left")])],"isStart":false});
            var Q10;
            Q10=makeQuery(id+"F2.opExtrude","CAP_EDGE",EDGE,{"disambiguationData":[OSD([sQuery(id+"F0.wireOp",EDGE,"E0.left")])],"isStart":false});
            var Q11;
            {var subQ0=sQuery(id+"F0.wireOp",EDGE,"E0.bottom");Q11=makeQuery(id+"F2.opExtrude","CAP_EDGE",EDGE,{"disambiguationData":[OSD([subQ0]),TDD([makeQuery(id+"F0.imprint","IMPRINT",EDGE,{"disambiguationData":[TD([[makeQuery(id+"F0.imprint","INTERSECT",VERTEX,{"derivedFrom":[subQ0,sQuery(id+"F0.wireOp",EDGE,"E0.left")]}),-1.0]])],"derivedFrom":subQ0})])],"isStart":false});}
            var Q12;
            {var subQ0=sQuery(id+"F0.wireOp",EDGE,"E1.left");Q12=makeQuery(id+"F2.opExtrude","CAP_EDGE",EDGE,{"disambiguationData":[OSD([subQ0]),TDD([makeQuery(id+"F0.imprint","IMPRINT",EDGE,{"disambiguationData":[TD([[makeQuery(id+"F0.imprint","INTERSECT",VERTEX,{"derivedFrom":[sQuery(id+"F0.wireOp",EDGE,"E1.top"),subQ0]}),1.0]])],"derivedFrom":subQ0})])],"isStart":false});}
            var Q13;
            {var subQ0=sQuery(id+"F0.wireOp",EDGE,"E1.top");Q13=makeQuery(id+"F2.opExtrude","CAP_EDGE",EDGE,{"disambiguationData":[OSD([subQ0]),TDD([makeQuery(id+"F0.imprint","IMPRINT",EDGE,{"disambiguationData":[TD([[makeQuery(id+"F0.imprint","INTERSECT",VERTEX,{"derivedFrom":[subQ0,sQuery(id+"F0.wireOp",EDGE,"E1.left")]}),-1.0]])],"derivedFrom":subQ0})])],"isStart":false});}
            var Q14;
            {var subQ0=sQuery(id+"F0.wireOp",EDGE,"E1.top");Q14=makeQuery(id+"F2.opExtrude","CAP_EDGE",EDGE,{"disambiguationData":[OSD([subQ0]),TDD([makeQuery(id+"F0.imprint","IMPRINT",EDGE,{"disambiguationData":[TD([[makeQuery(id+"F0.imprint","INTERSECT",VERTEX,{"derivedFrom":[subQ0,sQuery(id+"F0.wireOp",EDGE,"E1.right")]}),1.0]])],"derivedFrom":subQ0})])],"isStart":false});}
            var Q15;
            {var subQ0=sQuery(id+"F0.wireOp",EDGE,"E1.right");Q15=makeQuery(id+"F2.opExtrude","CAP_EDGE",EDGE,{"disambiguationData":[OSD([subQ0]),TDD([makeQuery(id+"F0.imprint","IMPRINT",EDGE,{"disambiguationData":[TD([[makeQuery(id+"F0.imprint","INTERSECT",VERTEX,{"derivedFrom":[sQuery(id+"F0.wireOp",EDGE,"E1.top"),subQ0]}),1.0]])],"derivedFrom":subQ0})])],"isStart":false});}
            chamfer(context, id + "F8", {"entities" : qUnion([Q0, Q1, Q2, Q3, Q4, Q5, Q6, Q7, Q8, Q9, Q10, Q11, Q12, Q13, Q14, Q15]), "width" : 2 * mm, "tangentPropagation" : true});
        }
    });
